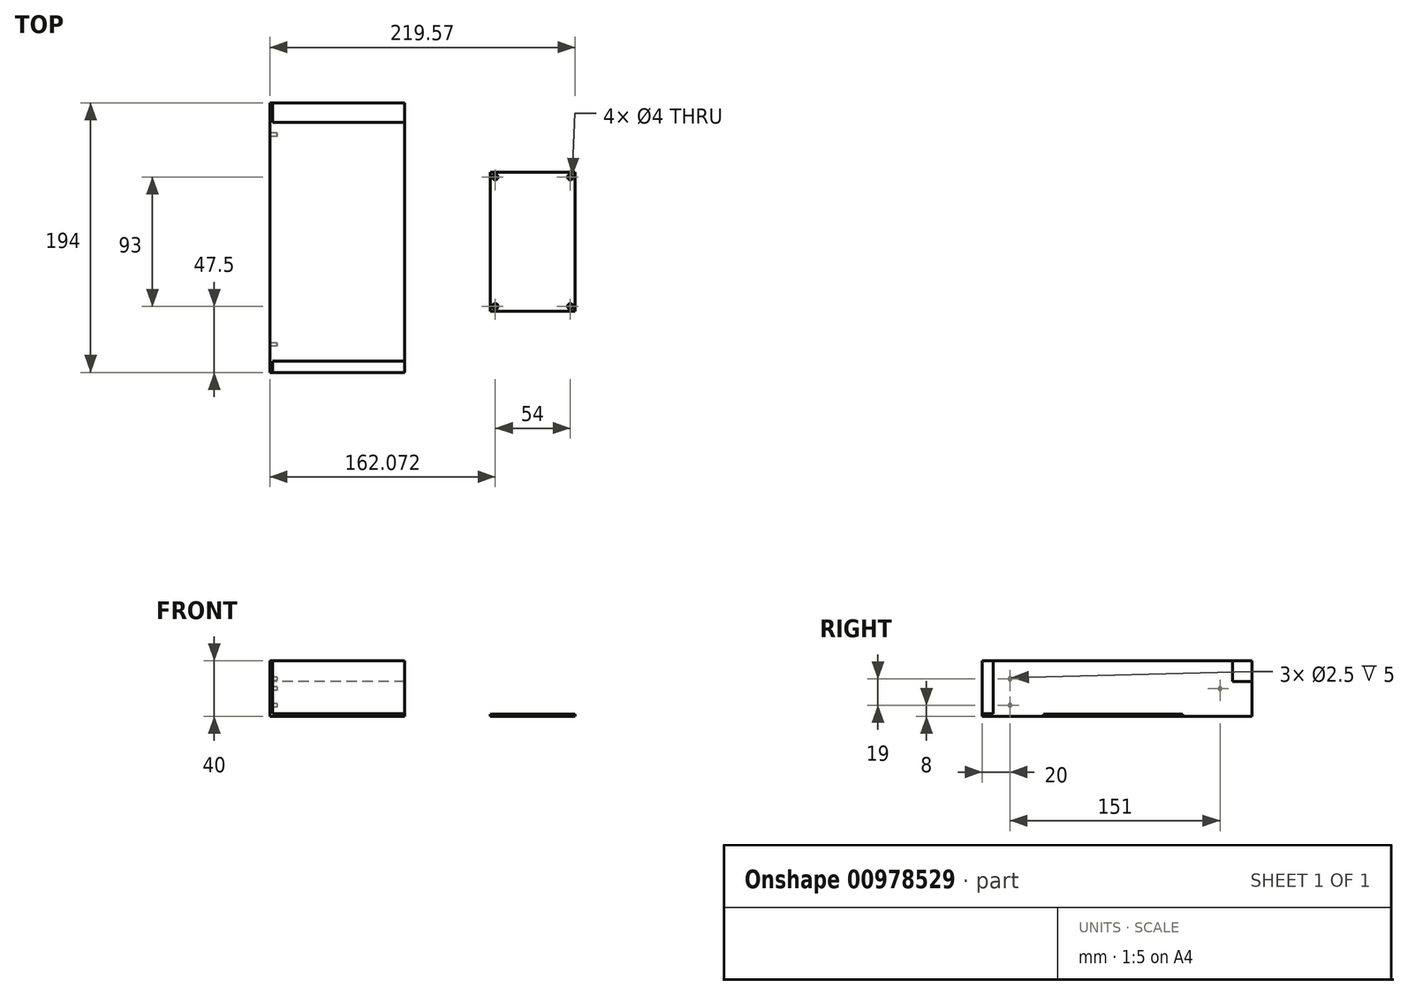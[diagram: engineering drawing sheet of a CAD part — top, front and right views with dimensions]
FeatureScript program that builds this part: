
annotation { "Feature Type Name" : "Feature", "Feature Type Description" : "" }
export const myFeature = defineFeature(function(context is Context, id is Id, definition is map)
    precondition{}
    {
        {
            var Q0;
            Q0=qCreatedBy(makeId("Top.planeOp"),FACE);
            var sketch = newSketch(context, id + "F0", { "sketchPlane" : qUnion([Q0])});
            skLineSegment(sketch, "E0.bottom", {"start": v(9.9, 86) * mm, "end": v(-87.1, 86) * mm});
            skLineSegment(sketch, "E0.top", {"start": v(9.9, -86) * mm, "end": v(-87.1, -86) * mm});
            skLineSegment(sketch, "E0.left", {"start": v(9.9, 86) * mm, "end": v(9.9, -86) * mm});
            skLineSegment(sketch, "E0.right", {"start": v(-87.1, 86) * mm, "end": v(-87.1, -86) * mm});
            skPoint(sketch, "E0.middle", {"position": v(-38.6, 0) * mm});
            skLineSegment(sketch, "E1", {"start": v(-87.1, 100) * mm, "end": v(9.9, 100) * mm});
            skLineSegment(sketch, "E2", {"start": v(-87.1, 86) * mm, "end": v(-87.1, 100) * mm});
            skLineSegment(sketch, "E3", {"start": v(9.9, 86) * mm, "end": v(9.9, 100) * mm});
            skLineSegment(sketch, "E4.bottom", {"start": v(-87.1, -86) * mm, "end": v(9.9, -86) * mm});
            skLineSegment(sketch, "E4.top", {"start": v(-87.1, -94) * mm, "end": v(9.9, -94) * mm});
            skLineSegment(sketch, "E4.left", {"start": v(-87.1, -86) * mm, "end": v(-87.1, -94) * mm});
            skLineSegment(sketch, "E4.right", {"start": v(9.9, -86) * mm, "end": v(9.9, -94) * mm});
            skLineSegment(sketch, "E5", {"start": v(-85.1, 100) * mm, "end": v(-85.1, 86) * mm});
            skLineSegment(sketch, "E6", {"start": v(-85.1, -86) * mm, "end": v(-85.1, -94) * mm});
            skLineSegment(sketch, "E7.bottom", {"start": v(132.46, 50) * mm, "end": v(71.46, 50) * mm});
            skLineSegment(sketch, "E7.top", {"start": v(132.46, -50) * mm, "end": v(71.46, -50) * mm});
            skLineSegment(sketch, "E7.left", {"start": v(132.46, 50) * mm, "end": v(132.46, -50) * mm});
            skLineSegment(sketch, "E7.right", {"start": v(71.46, 50) * mm, "end": v(71.46, -50) * mm});
            skPoint(sketch, "E7.middle", {"position": v(101.96, 0) * mm});
            skCircle(sketch, "E8", {"center": v(74.96, 46.5) * mm, "radius": 2 * mm});
            skLineSegment(sketch, "E9", {"start": v(132.46, 0) * mm, "end": v(71.46, 0) * mm, "construction": true});
            skLineSegment(sketch, "E10", {"start": v(101.96, 50) * mm, "end": v(101.96, -50) * mm, "construction": true});
            skCircle(sketch, "E11.MirrorC", {"center": v(128.96, 46.5) * mm, "radius": 2 * mm});
            skCircle(sketch, "E12.MirrorC", {"center": v(74.96, -46.5) * mm, "radius": 2 * mm});
            skCircle(sketch, "E13.MirrorC", {"center": v(128.96, -46.5) * mm, "radius": 2 * mm});
            skSolve(sketch);
        }
        {
            var Q0;
            Q0=makeQuery(id+"F0.imprint","IMPRINT",FACE,{"disambiguationData":[TD([[makeQuery(id+"F0.imprint","IMPRINT",EDGE,{"derivedFrom":sQuery(id+"F0.wireOp",EDGE,"E0.bottom")}),1.0]])]});
            var Q1;
            {var subQ0=sQuery(id+"F0.wireOp",EDGE,"E2");Q1=makeQuery(id+"F0.imprint","IMPRINT",FACE,{"disambiguationData":[TD([[makeQuery(id+"F0.imprint","IMPRINT",EDGE,{"derivedFrom":subQ0}),-1.0]])]});}
            var Q2;
            {var subQ0=sQuery(id+"F0.wireOp",EDGE,"E4.left");Q2=makeQuery(id+"F0.imprint","IMPRINT",FACE,{"disambiguationData":[TD([[makeQuery(id+"F0.imprint","IMPRINT",EDGE,{"derivedFrom":subQ0}),1.0]])]});}
            extrude(context, id + "F1", {"entities" : qUnion([Q0, Q1, Q2]), "flatOperationType" : FlatOperationType.REMOVE, "depth" : 40 * mm, "offsetDistance" : 25 * mm, "domain" : OperationDomain.MODEL});
        }
        {
            var Q0;
            {var subQ0=sQuery(id+"F0.wireOp",EDGE,"E4.right");Q0=makeQuery(id+"F0.imprint","IMPRINT",FACE,{"disambiguationData":[TD([[makeQuery(id+"F0.imprint","IMPRINT",EDGE,{"derivedFrom":subQ0}),-1.0]])]});}
            extrude(context, id + "F2", {"entities" : qUnion([Q0]), "operationType" : NewBodyOperationType.ADD, "depth" : 2 * mm, "offsetDistance" : 25 * mm});
        }
        {
            var Q0;
            {var subQ0=sQuery(id+"F0.wireOp",EDGE,"E3");Q0=makeQuery(id+"F0.imprint","IMPRINT",FACE,{"disambiguationData":[TD([[makeQuery(id+"F0.imprint","IMPRINT",EDGE,{"derivedFrom":subQ0}),1.0]])]});}
            extrude(context, id + "F3", {"entities" : qUnion([Q0]), "operationType" : NewBodyOperationType.ADD, "depth" : 25 * mm, "offsetDistance" : 25 * mm});
        }
        {
            var Q0;
            Q0=makeQuery(id+"F1.opExtrude","SWEPT_FACE",FACE,{"disambiguationData":[OSD([sQuery(id+"F0.wireOp",EDGE,"E0.right"),sQuery(id+"F0.wireOp",EDGE,"E2"),sQuery(id+"F0.wireOp",EDGE,"E4.left")])]});
            var sketch = newSketch(context, id + "F4", { "sketchPlane" : qUnion([Q0])});
            skCircle(sketch, "E14", {"center": v(74, 8) * mm, "radius": 1.25 * mm});
            skCircle(sketch, "E15", {"center": v(74, 27) * mm, "radius": 1.25 * mm});
            skCircle(sketch, "E16", {"center": v(-77, 20) * mm, "radius": 1.25 * mm});
            skPoint(sketch, "E17", {"position": v(-100, 20) * mm});
            skSolve(sketch);
        }
        {
            var Q0;
            Q0=makeQuery(id+"F4.imprint","IMPRINT",FACE,{"disambiguationData":[TD([[makeQuery(id+"F4.imprint","IMPRINT",EDGE,{"derivedFrom":sQuery(id+"F4.wireOp",EDGE,"E14")}),1.0]])]});
            var Q1;
            Q1=makeQuery(id+"F4.imprint","IMPRINT",FACE,{"disambiguationData":[TD([[makeQuery(id+"F4.imprint","IMPRINT",EDGE,{"derivedFrom":sQuery(id+"F4.wireOp",EDGE,"E15")}),1.0]])]});
            var Q2;
            Q2=makeQuery(id+"F4.imprint","IMPRINT",FACE,{"disambiguationData":[TD([[makeQuery(id+"F4.imprint","IMPRINT",EDGE,{"derivedFrom":sQuery(id+"F4.wireOp",EDGE,"E16")}),1.0]])]});
            extrude(context, id + "F5", {"entities" : qUnion([Q0, Q1, Q2]), "operationType" : NewBodyOperationType.REMOVE, "oppositeDirection" : true, "depth" : 5 * mm, "offsetDistance" : 25 * mm});
        }
        {
            var Q0;
            Q0=makeQuery(id+"F0.imprint","IMPRINT",FACE,{"disambiguationData":[TD([[makeQuery(id+"F0.imprint","IMPRINT",EDGE,{"derivedFrom":sQuery(id+"F0.wireOp",EDGE,"E7.bottom")}),1.0]])]});
            extrude(context, id + "F6", {"entities" : qUnion([Q0]), "depth" : 1.5 * mm, "offsetDistance" : 25 * mm});
        }
    });
